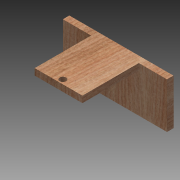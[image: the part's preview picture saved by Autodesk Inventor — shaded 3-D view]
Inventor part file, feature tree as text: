
AUTODESK INVENTOR PART (.ipt)
format: ipt  version: 2014 SP1 (Build 180222100, 222)  size: 110,592 bytes
history: native  units: in
note: dims shown in document units (in); Inventor stores cm internally (conversion verified against a paired STEP export)
features: extrude x3, sketch x3
ambient origin geometry x8: Origin, YZ Plane, XZ Plane, XY Plane, X Axis, Y Axis, Z Axis, Center Point
bodies: Solid1 (feature_tree)
feature tree (6):
  extrude  "Extrusion1"  Depth=5.25in
  extrude  "Extrusion2"  Depth=5.5in
  extrude  "Extrusion3"  Depth=3.25in
  sketch  "Sketch1"  dims[d0=12.0in d1=5.25in]
  sketch  "Sketch2"  dims[d2=0.75in d3=0.0in d4=5.5in]
  sketch  "Sketch3"  dims[d5=0.75in d6=3.25in d7=6.5in d8=0.0in d9=0.75in d10=0.5in d11=6.5in d12=0.0in]
